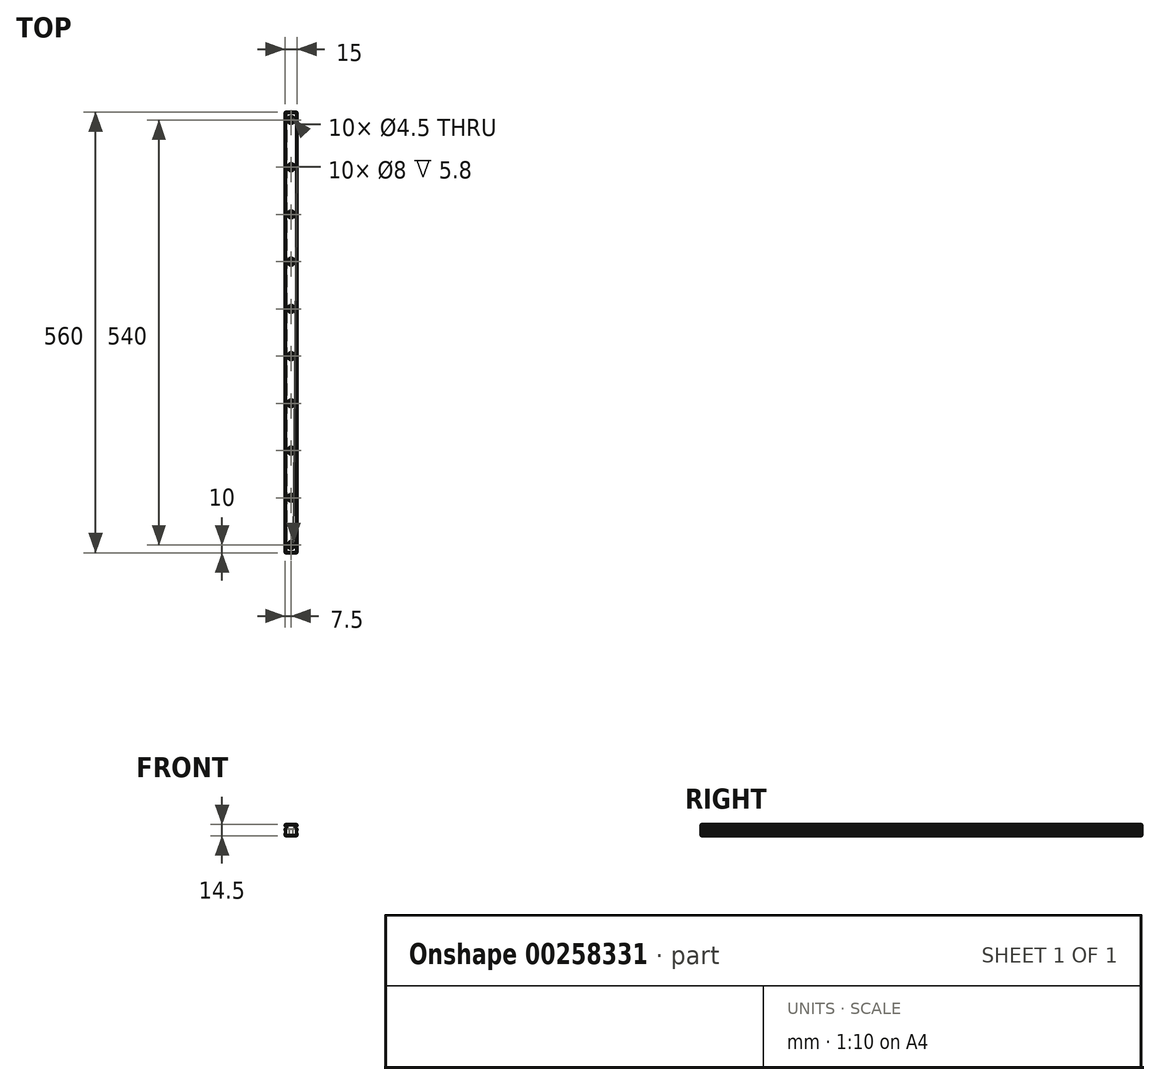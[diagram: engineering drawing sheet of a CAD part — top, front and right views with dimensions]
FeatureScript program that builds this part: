
annotation { "Feature Type Name" : "Feature", "Feature Type Description" : "" }
export const myFeature = defineFeature(function(context is Context, id is Id, definition is map)
    precondition{}
    {
        {
            var Q0;
            Q0=qCreatedBy(makeId("Front.planeOp"),FACE);
            var sketch = newSketch(context, id + "F0", { "sketchPlane" : qUnion([Q0])});
            skLineSegment(sketch, "E0", {"start": v(0, 7.25) * mm, "end": v(0, -7.25) * mm, "construction": true});
            skLineSegment(sketch, "E1", {"start": v(0, -7.25) * mm, "end": v(-7.5, -7.25) * mm});
            skLineSegment(sketch, "E2", {"start": v(-7.5, -7.25) * mm, "end": v(-7.5, -4.13) * mm});
            skLineSegment(sketch, "E3", {"start": v(-7.5, -4.13) * mm, "end": v(-7.5, -4.13) * mm});
            skLineSegment(sketch, "E4", {"start": v(-6.8, -3.43) * mm, "end": v(-6.8, -0.7) * mm});
            skLineSegment(sketch, "E5", {"start": v(-7.5, 0) * mm, "end": v(-7.5, 0) * mm});
            skLineSegment(sketch, "E6", {"start": v(-7.5, 0) * mm, "end": v(-7.5, 1.88) * mm});
            skLineSegment(sketch, "E7", {"start": v(-7.5, 1.88) * mm, "end": v(-7.5, 1.88) * mm});
            skLineSegment(sketch, "E8", {"start": v(-6.8, 2.88) * mm, "end": v(-5.5, 2.88) * mm});
            skLineSegment(sketch, "E9", {"start": v(-5.5, 2.88) * mm, "end": v(-5.5, 4.38) * mm});
            skLineSegment(sketch, "E10", {"start": v(-5.5, 4.38) * mm, "end": v(-6.8, 4.38) * mm});
            skLineSegment(sketch, "E11", {"start": v(-6.8, 4.38) * mm, "end": v(-6.8, 4.68) * mm});
            skLineSegment(sketch, "E12", {"start": v(-7.5, 5.38) * mm, "end": v(-7.5, 5.38) * mm});
            skLineSegment(sketch, "E13", {"start": v(-7.5, 5.38) * mm, "end": v(-7.5, 7.25) * mm});
            skLineSegment(sketch, "E14", {"start": v(-7.5, 7.25) * mm, "end": v(0, 7.25) * mm});
            skLineSegment(sketch, "E15", {"start": v(-6.8, 2.58) * mm, "end": v(-6.8, 2.87) * mm});
            skPoint(sketch, "E16.visualSharp", {"position": v(-6.8, -4.13) * mm});
            skArc(sketch, "E16.filletArc", {"start": v(-7.5, -4.13) * mm, "mid": v(-7, -3.92) * mm, "end": v(-6.8, -3.43) * mm});
            skPoint(sketch, "E17.visualSharp", {"position": v(-6.8, 0) * mm});
            skArc(sketch, "E17.filletArc", {"start": v(-6.8, -0.7) * mm, "mid": v(-7, -0.2) * mm, "end": v(-7.5, 0) * mm});
            skPoint(sketch, "E18.visualSharp", {"position": v(-6.8, 1.88) * mm});
            skArc(sketch, "E18.filletArc", {"start": v(-7.5, 1.88) * mm, "mid": v(-7, 2.08) * mm, "end": v(-6.8, 2.58) * mm});
            skPoint(sketch, "E19.visualSharp", {"position": v(-6.8, 5.38) * mm});
            skArc(sketch, "E19.filletArc", {"start": v(-6.8, 4.68) * mm, "mid": v(-7, 5.17) * mm, "end": v(-7.5, 5.38) * mm});
            skLineSegment(sketch, "E20.MirrorCS", {"start": v(6.8, 2.58) * mm, "end": v(6.8, 2.87) * mm});
            skLineSegment(sketch, "E21.MirrorCS", {"start": v(6.8, 4.38) * mm, "end": v(6.8, 4.68) * mm});
            skArc(sketch, "E22.MirrorCS", {"start": v(6.8, 4.68) * mm, "mid": v(7, 5.17) * mm, "end": v(7.5, 5.38) * mm});
            skArc(sketch, "E23.MirrorCS", {"start": v(7.5, 1.88) * mm, "mid": v(7, 2.08) * mm, "end": v(6.8, 2.58) * mm});
            skArc(sketch, "E24.MirrorCS", {"start": v(7.5, -4.13) * mm, "mid": v(7, -3.92) * mm, "end": v(6.8, -3.43) * mm});
            skArc(sketch, "E25.MirrorCS", {"start": v(6.8, -0.7) * mm, "mid": v(7, -0.2) * mm, "end": v(7.5, 0) * mm});
            skLineSegment(sketch, "E26.MirrorCS", {"start": v(7.5, 0) * mm, "end": v(7.5, 0) * mm});
            skLineSegment(sketch, "E27.MirrorCS", {"start": v(7.5, -7.25) * mm, "end": v(7.5, -4.13) * mm});
            skPoint(sketch, "E28.MirrorP", {"position": v(6.8, 0) * mm});
            skPoint(sketch, "E29.MirrorP", {"position": v(6.8, 5.38) * mm});
            skPoint(sketch, "E30.MirrorP", {"position": v(6.8, 1.88) * mm});
            skLineSegment(sketch, "E31.MirrorCS", {"start": v(7.5, -4.13) * mm, "end": v(7.5, -4.13) * mm});
            skLineSegment(sketch, "E32.MirrorCS", {"start": v(7.5, 1.88) * mm, "end": v(7.5, 1.88) * mm});
            skLineSegment(sketch, "E33.MirrorCS", {"start": v(7.5, 5.38) * mm, "end": v(7.5, 5.38) * mm});
            skLineSegment(sketch, "E34.MirrorCS", {"start": v(7.5, 5.38) * mm, "end": v(7.5, 7.25) * mm});
            skLineSegment(sketch, "E35.MirrorCS", {"start": v(5.5, 4.38) * mm, "end": v(6.8, 4.38) * mm});
            skLineSegment(sketch, "E36.MirrorCS", {"start": v(6.8, -3.43) * mm, "end": v(6.8, -0.7) * mm});
            skPoint(sketch, "E37.MirrorP", {"position": v(6.8, -4.13) * mm});
            skLineSegment(sketch, "E38.MirrorCS", {"start": v(6.8, 2.88) * mm, "end": v(5.5, 2.88) * mm});
            skLineSegment(sketch, "E39.MirrorCS", {"start": v(7.5, 0) * mm, "end": v(7.5, 1.88) * mm});
            skLineSegment(sketch, "E40.MirrorCS", {"start": v(5.5, 2.88) * mm, "end": v(5.5, 4.38) * mm});
            skLineSegment(sketch, "E41.MirrorCS", {"start": v(7.5, 7.25) * mm, "end": v(0, 7.25) * mm});
            skLineSegment(sketch, "E42.MirrorCS", {"start": v(0, -7.25) * mm, "end": v(7.5, -7.25) * mm});
            skSolve(sketch);
        }
        {
            var Q0;
            Q0=qSketchRegion(id+"F0",true);
            extrude(context, id + "F1", {"entities" : qUnion([Q0]), "oppositeDirection" : true, "depth" : 560 * mm});
        }
        {
            var Q0;
            Q0=makeQuery(id+"F1.opExtrude","SWEPT_FACE",FACE,{"disambiguationData":[OSD([sQuery(id+"F0.wireOp",EDGE,"E14"),sQuery(id+"F0.wireOp",EDGE,"E41.MirrorCS")])]});
            var sketch = newSketch(context, id + "F2", { "sketchPlane" : qUnion([Q0])});
            skLineSegment(sketch, "E43", {"start": v(0, 0) * mm, "end": v(0, 560) * mm, "construction": true});
            skCircle(sketch, "E44", {"center": v(0, 10) * mm, "radius": 2.25 * mm});
            skCircle(sketch, "E45", {"center": v(0, 70) * mm, "radius": 2.25 * mm});
            skCircle(sketch, "E46", {"center": v(0, 130) * mm, "radius": 2.25 * mm});
            skCircle(sketch, "E47", {"center": v(0, 190) * mm, "radius": 2.25 * mm});
            skCircle(sketch, "E48", {"center": v(0, 250) * mm, "radius": 2.25 * mm});
            skCircle(sketch, "E49", {"center": v(0, 310) * mm, "radius": 2.25 * mm});
            skCircle(sketch, "E50", {"center": v(0, 370) * mm, "radius": 2.25 * mm});
            skCircle(sketch, "E51", {"center": v(0, 430) * mm, "radius": 2.25 * mm});
            skCircle(sketch, "E52", {"center": v(0, 490) * mm, "radius": 2.25 * mm});
            skCircle(sketch, "E53", {"center": v(0, 550) * mm, "radius": 2.25 * mm});
            skSolve(sketch);
        }
        {
            var Q0;
            Q0=qSketchRegion(id+"F2",true);
            extrude(context, id + "F3", {"entities" : qUnion([Q0]), "operationType" : NewBodyOperationType.REMOVE, "endBound" : BoundingType.UP_TO_NEXT, "oppositeDirection" : true, "depth" : 25 * mm});
        }
        {
            var Q0;
            Q0=makeQuery(id+"F1.opExtrude","SWEPT_FACE",FACE,{"disambiguationData":[OSD([sQuery(id+"F0.wireOp",EDGE,"E14"),sQuery(id+"F0.wireOp",EDGE,"E41.MirrorCS")])]});
            var sketch = newSketch(context, id + "F4", { "sketchPlane" : qUnion([Q0])});
            skCircle(sketch, "E54", {"center": v(0, 10) * mm, "radius": 4 * mm});
            skCircle(sketch, "E55", {"center": v(0, 70) * mm, "radius": 4 * mm});
            skCircle(sketch, "E56", {"center": v(0, 130) * mm, "radius": 4 * mm});
            skCircle(sketch, "E57", {"center": v(0, 190) * mm, "radius": 4 * mm});
            skCircle(sketch, "E58", {"center": v(0, 250) * mm, "radius": 4 * mm});
            skCircle(sketch, "E59", {"center": v(0, 310) * mm, "radius": 4 * mm});
            skCircle(sketch, "E60", {"center": v(0, 370) * mm, "radius": 4 * mm});
            skCircle(sketch, "E61", {"center": v(0, 430) * mm, "radius": 4 * mm});
            skCircle(sketch, "E62", {"center": v(0, 490) * mm, "radius": 4 * mm});
            skCircle(sketch, "E63", {"center": v(0, 550) * mm, "radius": 4 * mm});
            skSolve(sketch);
        }
        {
            var Q0;
            Q0=qSketchRegion(id+"F4",true);
            extrude(context, id + "F5", {"entities" : qUnion([Q0]), "operationType" : NewBodyOperationType.REMOVE, "oppositeDirection" : true, "depth" : 6.3 * mm});
        }
        {
            var Q0;
            Q0=makeQuery(id+"F1.opExtrude","SWEPT_FACE",FACE,{"disambiguationData":[OSD([sQuery(id+"F0.wireOp",EDGE,"E14"),sQuery(id+"F0.wireOp",EDGE,"E41.MirrorCS")])]});
            var Q1;
            Q1=makeQuery(id+"F1.opExtrude","SWEPT_FACE",FACE,{"disambiguationData":[OSD([sQuery(id+"F0.wireOp",EDGE,"E1"),sQuery(id+"F0.wireOp",EDGE,"E42.MirrorCS")])]});
            var Q2;
            Q2=makeQuery(id+"F1.opExtrude","CAP_EDGE",EDGE,{"disambiguationData":[OSD([sQuery(id+"F0.wireOp",EDGE,"E13")])],"isStart":true});
            var Q3;
            Q3=makeQuery(id+"F1.opExtrude","CAP_EDGE",EDGE,{"disambiguationData":[OSD([sQuery(id+"F0.wireOp",EDGE,"E6")])],"isStart":true});
            var Q4;
            Q4=makeQuery(id+"F1.opExtrude","CAP_EDGE",EDGE,{"disambiguationData":[OSD([sQuery(id+"F0.wireOp",EDGE,"E2")])],"isStart":true});
            var Q5;
            Q5=makeQuery(id+"F1.opExtrude","CAP_EDGE",EDGE,{"disambiguationData":[OSD([sQuery(id+"F0.wireOp",EDGE,"E27.MirrorCS")])],"isStart":true});
            var Q6;
            Q6=makeQuery(id+"F1.opExtrude","CAP_EDGE",EDGE,{"disambiguationData":[OSD([sQuery(id+"F0.wireOp",EDGE,"E39.MirrorCS")])],"isStart":true});
            var Q7;
            Q7=makeQuery(id+"F1.opExtrude","CAP_EDGE",EDGE,{"disambiguationData":[OSD([sQuery(id+"F0.wireOp",EDGE,"E34.MirrorCS")])],"isStart":true});
            var Q8;
            Q8=makeQuery(id+"F1.opExtrude","CAP_EDGE",EDGE,{"disambiguationData":[OSD([sQuery(id+"F0.wireOp",EDGE,"E2")])],"isStart":false});
            var Q9;
            Q9=makeQuery(id+"F1.opExtrude","CAP_EDGE",EDGE,{"disambiguationData":[OSD([sQuery(id+"F0.wireOp",EDGE,"E6")])],"isStart":false});
            var Q10;
            Q10=makeQuery(id+"F1.opExtrude","CAP_EDGE",EDGE,{"disambiguationData":[OSD([sQuery(id+"F0.wireOp",EDGE,"E13")])],"isStart":false});
            var Q11;
            Q11=makeQuery(id+"F1.opExtrude","CAP_EDGE",EDGE,{"disambiguationData":[OSD([sQuery(id+"F0.wireOp",EDGE,"E34.MirrorCS")])],"isStart":false});
            var Q12;
            Q12=makeQuery(id+"F1.opExtrude","CAP_EDGE",EDGE,{"disambiguationData":[OSD([sQuery(id+"F0.wireOp",EDGE,"E39.MirrorCS")])],"isStart":false});
            var Q13;
            Q13=makeQuery(id+"F1.opExtrude","CAP_EDGE",EDGE,{"disambiguationData":[OSD([sQuery(id+"F0.wireOp",EDGE,"E27.MirrorCS")])],"isStart":false});
            chamfer(context, id + "F6", {"entities" : qUnion([Q0, Q1, Q2, Q3, Q4, Q5, Q6, Q7, Q8, Q9, Q10, Q11, Q12, Q13]), "width" : 0.5 * mm, "tangentPropagation" : true});
        }
    });
